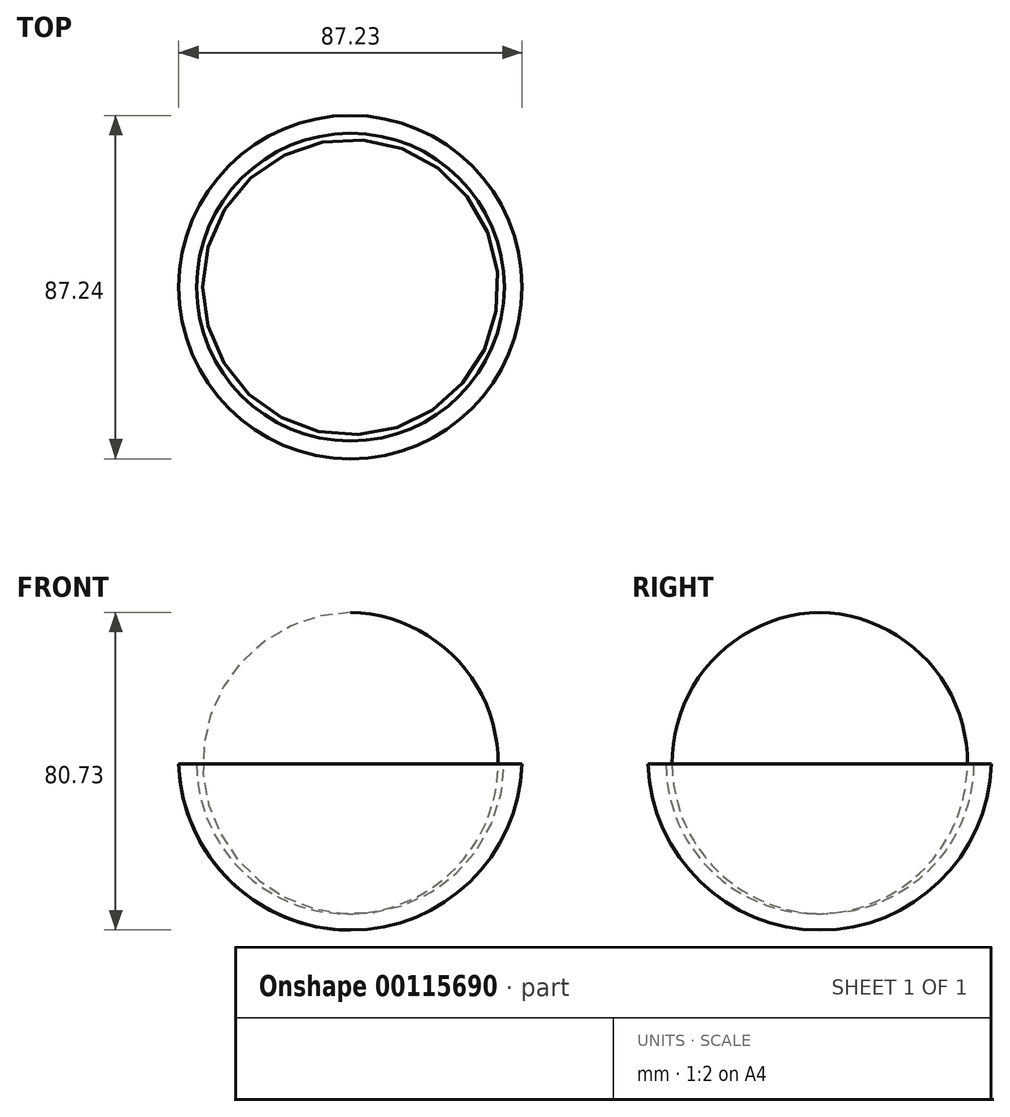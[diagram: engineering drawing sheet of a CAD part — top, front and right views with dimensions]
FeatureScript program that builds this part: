
annotation { "Feature Type Name" : "Feature", "Feature Type Description" : "" }
export const myFeature = defineFeature(function(context is Context, id is Id, definition is map)
    precondition{}
    {
        {
            var Q0;
            Q0=qCreatedBy(makeId("Front.planeOp"),FACE);
            var sketch = newSketch(context, id + "F0", { "sketchPlane" : qUnion([Q0])});
            skArc(sketch, "E0", {"start": v(-46.72, 0) * mm, "mid": v(-33.44, -29.9) * mm, "end": v(-3.1, -42.16) * mm});
            skPoint(sketch, "E1.visualSharp", {"position": v(-3.1, 68.81) * mm});
            skArc(sketch, "E2", {"start": v(-46.72, 0) * mm, "mid": v(-38.44, 36.12) * mm, "end": v(-13.34, 63.39) * mm});
            skArc(sketch, "E3.filletArc", {"start": v(-3.1, 66.37) * mm, "mid": v(-8.44, 65.61) * mm, "end": v(-13.34, 63.39) * mm});
            skLineSegment(sketch, "E4", {"start": v(-3.1, 66.37) * mm, "end": v(-3.1, 61.4) * mm});
            skPoint(sketch, "E5.orphan", {"position": v(40.51, 0) * mm});
            skArc(sketch, "E6", {"start": v(-42.2, 0) * mm, "mid": v(-30.6, -27.19) * mm, "end": v(-3.1, -38.03) * mm});
            skPoint(sketch, "E7.orphan", {"position": v(34.41, 0) * mm});
            skArc(sketch, "E8", {"start": v(-42.2, 0) * mm, "mid": v(-31.72, 36.47) * mm, "end": v(-3.1, 61.4) * mm});
            skLineSegment(sketch, "E9.trimOffspring", {"start": v(-3.1, -38.03) * mm, "end": v(-3.1, -42.16) * mm});
            skLineSegment(sketch, "E10", {"start": v(-46.72, 0) * mm, "end": v(-42.2, 0) * mm});
            skLineSegment(sketch, "E11", {"start": v(-3.1, 66.37) * mm, "end": v(-3.1, -42.16) * mm, "construction": true});
            skArc(sketch, "E12.MirrorCS", {"start": v(40.51, 0) * mm, "mid": v(32.23, 36.12) * mm, "end": v(7.13, 63.39) * mm, "construction": true});
            skArc(sketch, "E13.MirrorCS", {"start": v(-3.1, 66.37) * mm, "mid": v(2.23, 65.61) * mm, "end": v(7.13, 63.39) * mm, "construction": true});
            skArc(sketch, "E14.MirrorCS", {"start": v(40.51, 0) * mm, "mid": v(27.23, -29.9) * mm, "end": v(-3.1, -42.16) * mm, "construction": true});
            skText(sketch, "E15", { "text": "GCA", "fontName": "OpenSans-Regular.ttf"});
            const initialGuessF0  = {"E15": [-0.02112, 0.02402, 1, 0, 0.00804]};
            skSetInitialGuess(sketch, initialGuessF0);
            skSolve(sketch);
        }
        {
            var Q0;
            Q0=makeQuery(id+"F0.imprint","IMPRINT",FACE,{"disambiguationData":[TD([[makeQuery(id+"F0.imprint","IMPRINT",EDGE,{"derivedFrom":sQuery(id+"F0.wireOp",EDGE,"E0")}),1.0]])]});
            var Q1;
            Q1=makeQuery(id+"F0.imprint","IMPRINT",FACE,{"disambiguationData":[TD([[makeQuery(id+"F0.imprint","IMPRINT",EDGE,{"derivedFrom":sQuery(id+"F0.wireOp",EDGE,"E2")}),-1.0]])]});
            var Q2;
            Q2=sQuery(id+"F0.wireOp",EDGE,"E4");
            revolve(context, id + "F1", {"entities" : qUnion([Q0, Q1]), "axis" : qUnion([Q2]), "revolveType" : RevolveType.FULL});
        }
    });
